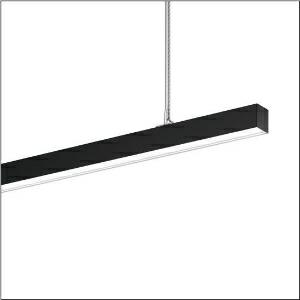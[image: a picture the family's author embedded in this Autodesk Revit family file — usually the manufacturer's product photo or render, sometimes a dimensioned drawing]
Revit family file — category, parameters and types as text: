
# Revit family: silica_r__21_51mx30dc49bb_d1ca
name_source: partatom
category: Lighting Fixtures
units: mm (PartAtom-declared; Revit-internal decimal feet)

## family parameters
Cut with Voids When Loaded = No
Host = Face
Light Source = No
Part Type = Normal
Room Calculation Point = No
Round Connector Dimension = Use Diameter
Shared = No

## types (1)
- --- (1 x LED, 10520 lm, 64.1 W, 4000K)
    Apparent Load = 64 VA
    CIE Flux Codes = 47 79 96 57 100
    Color Rendering = 80
    Color Temperature = 4000K
    Default Elevation = 1800 mm
    Description = Silica® 21, office luminaire, primary optical cover: cover, of PMMA, opal, light emission: direct/indirect distribution, primary light characteristic: symmetric, installation type: suspended mounting, LED, rated luminous flux: 10.520lm, luminous efficacy: 164lm/W, light colour: 840, colour temperature: 4000K, with terminal, 3+2-pole, max. 2.5mm², mains connection: 220..240V, AC, 50/60Hz, rated input power: 64.1W, luminaire housing, of aluminium, jet black (RAL 9005), length: 3.004mm, width: 53mm, height: 53mm, protection rating (complete): IP20, insulation class (complete): insulation class I (protective earthing), certification: CE, permissible operating ambient temperature: 0..+35°C, standard: EN 50419, packaging unit: 1 piece
    Height = 53 mm
    Lamp = 1 x LED
    Lamp Light Flux = 10520 lm
    Lamp Power = 64.1 W
    Lamp count = 1
    Length = 3004 mm
    Luminous efficacy = 164 lm/W
    Manufacturer = Siteco
    ModVariant = No
    Model = 51MX30DC49BB
    Mounting Place = Ceiling
    Mounting Type = Pendant
    Number of Poles = 1
    OnlyDefault = Yes
    Power Factor = 1
    Product Name = Silica® 21
    Product group = office luminaire | ceiling pendant
    ProductGroupID = 905
    Protection Class = Protection class I
    Protection Degree = IP 20
    RLX_Detail_Level = 1
    RlxData = <blob elided: 26041 chars, md5=a5c8dbe0>
    Socket = socket
    Standby Power = 0 W
    System Light Flux = 10520 lm
    System Power = 64 W
    Type Comments = factory setting: luminous flux: 100 % | dim-lin: 254 | 218 mA
    Type Image = l_1251735.jpg
    URL = http://relux.com
    VarID = @adj_025671
    Voltage = 0 V
    Weight = 0.00 kg
    Width = 53 mm

## geometry (parser evidence)
native form markers: Blend x4, Sweep x13
no freeform markers — native parametric forms only
